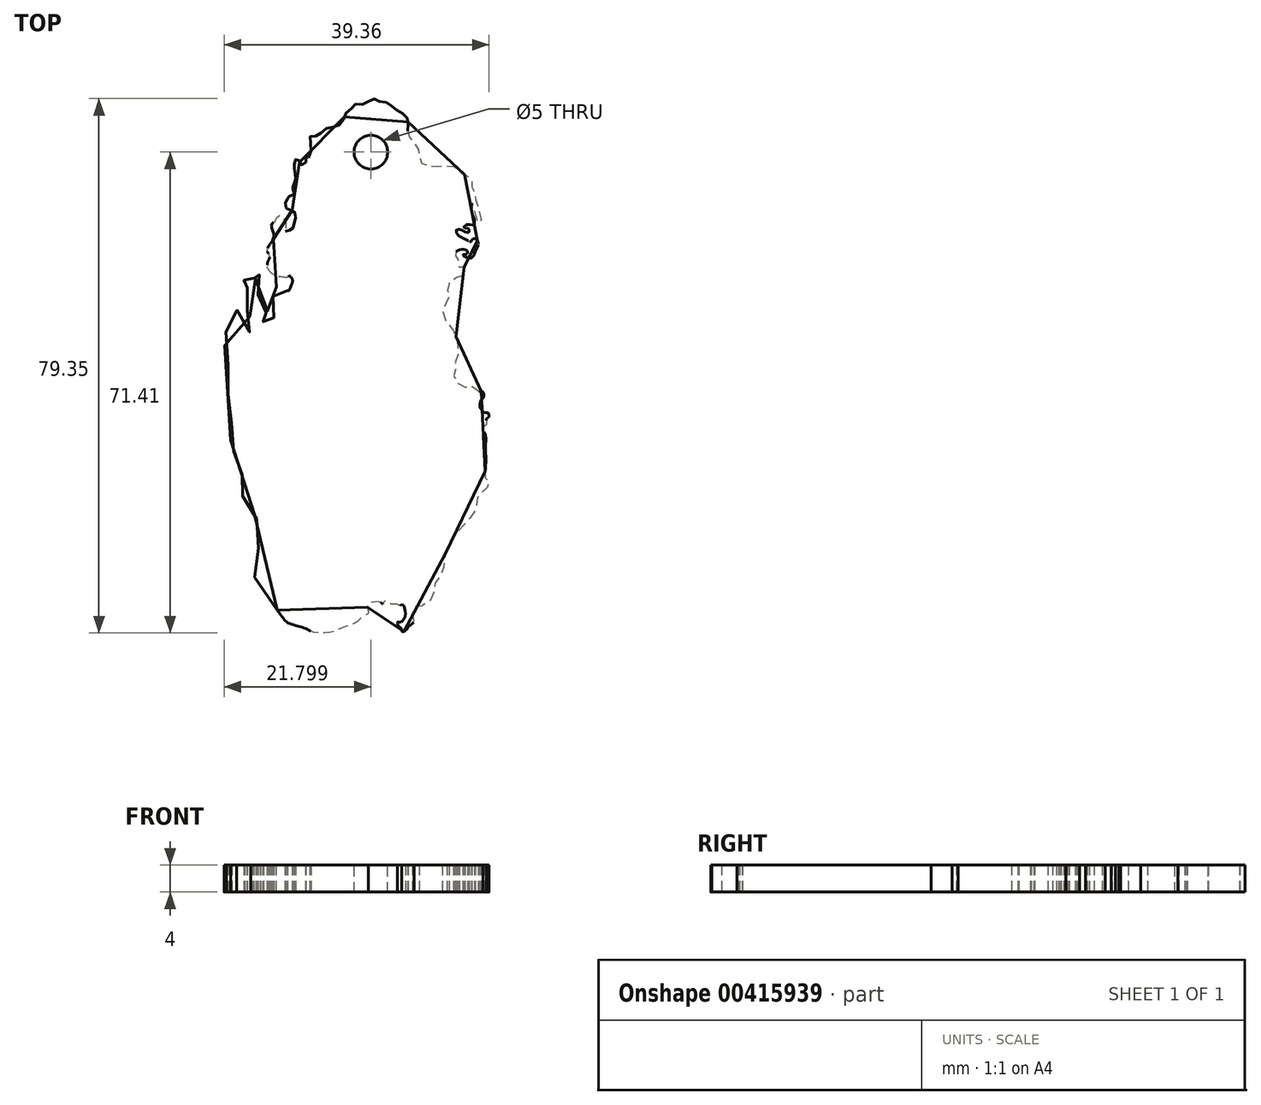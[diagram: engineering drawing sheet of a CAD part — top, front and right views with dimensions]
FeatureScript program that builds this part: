
annotation { "Feature Type Name" : "Feature", "Feature Type Description" : "" }
export const myFeature = defineFeature(function(context is Context, id is Id, definition is map)
    precondition{}
    {
        {
            var Q0;
            Q0=qCreatedBy(makeId("Top.planeOp"),FACE);
            var sketch = newSketch(context, id + "F0", { "sketchPlane" : qUnion([Q0])});
            skFitSpline(sketch, "E0", {"points": [v(-12.7, -36.37) * mm, v(-13.37, -35.26) * mm, v(-14.11, -34.04) * mm, v(-15.15, -32.77) * mm, v(-15.78, -31.92) * mm, v(-16.53, -30.77) * mm, v(-16.68, -30.32) * mm, v(-15.82, -29.47) * mm, v(-15.34, -28.62) * mm, v(-15.23, -27.72) * mm, v(-15.67, -26.9) * mm, v(-15.93, -26.28) * mm, v(-15.67, -25.6) * mm, v(-15.71, -24.87) * mm, v(-15.86, -24.05) * mm, v(-15.78, -23.08) * mm, v(-15.85, -22.68) * mm, v(-16.09, -22.18) * mm, v(-16.59, -21.6) * mm, v(-17.04, -21.1) * mm, v(-17.33, -20.57) * mm, v(-17.57, -19.8) * mm, v(-17.88, -19.43) * mm, v(-18.3, -18.85) * mm, v(-18.6, -18.32) * mm, v(-18.73, -17.72) * mm, v(-18.72, -17.32) * mm, v(-18.63, -16.98) * mm, v(-18.35, -16.53) * mm, v(-18.02, -16.25) * mm, v(-17.73, -15.87) * mm, v(-17.73, -15.4) * mm, v(-17.92, -14.7) * mm, v(-18.17, -14.08) * mm, v(-18.5, -13.6) * mm, v(-18.87, -13.08) * mm, v(-19.3, -12.58) * mm, v(-19.58, -12) * mm, v(-19.63, -11.03) * mm, v(-19.6, -10.14) * mm, v(-19.56, -9.28) * mm, v(-19.45, -8.78) * mm, v(-19.56, -8.51) * mm, v(-19.9, -8.13) * mm, v(-20.18, -7.51) * mm, v(-20.24, -6.57) * mm, v(-20.27, -5.7) * mm, v(-20.15, -4.8) * mm, v(-20, -4.01) * mm, v(-19.87, -3.27) * mm, v(-19.83, -2.2) * mm, v(-19.9, -1.14) * mm, v(-20, -0.58) * mm, v(-20.18, -0.24) * mm, v(-20.02, 0) * mm, v(-20.02, 1.35) * mm, v(-20.24, 2.32) * mm, v(-20.58, 3) * mm, v(-20.61, 3.77) * mm, v(-20.45, 4.76) * mm, v(-19.99, 5.75) * mm, v(-19.92, 6.55) * mm, v(-20.22, 6.64) * mm, v(-20.25, 7.07) * mm, v(-19.65, 7.7) * mm, v(-18.93, 8.1) * mm, v(-18.43, 8.23) * mm, v(-17.97, 7.87) * mm, v(-17.57, 6.94) * mm, v(-17.27, 6.31) * mm, v(-17.2, 5.69) * mm, v(-17.2, 5.12) * mm, v(-16.71, 4.96) * mm, v(-16.28, 5.16) * mm, v(-16.25, 5.52) * mm, v(-16.55, 6.02) * mm, v(-16.71, 6.31) * mm, v(-16.78, 7.07) * mm, v(-16.98, 7.77) * mm, v(-17.24, 8.1) * mm, v(-17.54, 8.3) * mm, v(-17.3, 8.9) * mm, v(-17.08, 9.35) * mm, v(-16.86, 9.86) * mm, v(-16.83, 10.44) * mm, v(-17.08, 11.16) * mm, v(-17.2, 11.6) * mm, v(-17.2, 11.93) * mm, v(-17.59, 11.85) * mm, v(-18, 11.7) * mm, v(-18.5, 11.67) * mm, v(-18.69, 11.93) * mm, v(-18.48, 12.36) * mm, v(-17.96, 12.57) * mm, v(-17.4, 12.71) * mm, v(-16.9, 12.69) * mm, v(-16.6, 12.55) * mm, v(-16.35, 12.23) * mm, v(-16.1, 12.07) * mm, v(-15.9, 12.14) * mm, v(-15.62, 12.31) * mm, v(-15.76, 12.65) * mm, v(-16.14, 13.03) * mm, v(-16.46, 13.3) * mm, v(-16.48, 13.97) * mm, v(-16.42, 14.4) * mm, v(-16.25, 14.4) * mm, v(-16.16, 14.1) * mm, v(-15.94, 13.89) * mm, v(-15.69, 13.74) * mm, v(-15.55, 13.53) * mm, v(-15.2, 13.47) * mm, v(-14.94, 13.47) * mm, v(-14.8, 12.85) * mm, v(-14.77, 12.3) * mm, v(-15.02, 11.76) * mm, v(-15.4, 11.2) * mm, v(-15.58, 10.82) * mm, v(-15.6, 10.44) * mm, v(-15.47, 10.32) * mm, v(-15.35, 10.36) * mm, v(-15.22, 9.95) * mm, v(-15.24, 9.36) * mm, v(-15.28, 8.85) * mm, v(-15.19, 8.44) * mm, v(-14.86, 8.04) * mm, v(-14.46, 7.87) * mm, v(-14.15, 7.94) * mm, v(-14.23, 8.26) * mm, v(-14.01, 8.36) * mm, v(-13.83, 7.99) * mm, v(-13.8, 7.7) * mm, v(-14.05, 7.33) * mm, v(-14.41, 7.02) * mm, v(-14.7, 6.78) * mm, v(-14.86, 6.2) * mm, v(-14.74, 5.88) * mm, v(-14.21, 6.05) * mm, v(-13.76, 5.94) * mm, v(-13.43, 6.01) * mm, v(-13.52, 6.5) * mm, v(-13.72, 7.02) * mm, v(-13.2, 7.1) * mm, v(-12.95, 7.47) * mm, v(-12.93, 7.74) * mm, v(-13.37, 7.8) * mm, v(-13.45, 8.37) * mm, v(-13.39, 9) * mm, v(-13.39, 9.73) * mm, v(-13.39, 10.24) * mm, v(-13, 10.85) * mm, v(-12.9, 11.58) * mm, v(-12.64, 12.19) * mm, v(-12.1, 12.3) * mm, v(-11.64, 11.95) * mm, v(-11.22, 11.34) * mm, v(-11.05, 11.07) * mm, v(-10.6, 11.96) * mm, v(-10.5, 12.76) * mm, v(-10.89, 13.3) * mm, v(-11.2, 13.08) * mm, v(-11.87, 13.13) * mm, v(-12.88, 13.27) * mm, v(-13.72, 13.86) * mm, v(-14.2, 14.72) * mm, v(-14.07, 15.56) * mm, v(-13.86, 16.08) * mm, v(-14.05, 16.62) * mm, v(-14.2, 17.08) * mm, v(-13.93, 17.84) * mm, v(-13.58, 18.32) * mm, v(-13.29, 18.93) * mm, v(-13.27, 19.6) * mm, v(-13.48, 20.27) * mm, v(-13.6, 20.76) * mm, v(-13.42, 21.15) * mm, v(-13.1, 21.31) * mm, v(-12.97, 21.57) * mm, v(-12.82, 21.95) * mm, v(-12.43, 22.22) * mm, v(-12.07, 22.23) * mm, v(-11.75, 21.86) * mm, v(-11.52, 21.42) * mm, v(-11.48, 20.8) * mm, v(-11.5, 20.24) * mm, v(-11.6, 19.95) * mm, v(-11.28, 19.9) * mm, v(-10.93, 20.06) * mm, v(-10.76, 20.34) * mm, v(-10.43, 20.39) * mm, v(-10.23, 20.82) * mm, v(-10.18, 21.37) * mm, v(-10.06, 21.77) * mm, v(-10, 22.21) * mm, v(-10.12, 22.75) * mm, v(-10.48, 23.07) * mm, v(-11.02, 23.12) * mm, v(-11.33, 23.3) * mm, v(-11.5, 23.67) * mm, v(-11.5, 24.14) * mm, v(-11.29, 24.58) * mm, v(-11.23, 24.91) * mm, v(-11.2, 25.12) * mm, v(-10.72, 25.12) * mm, v(-10.24, 25.37) * mm, v(-10.15, 25.7) * mm, v(-10.21, 25.83) * mm, v(-10.4, 25.94) * mm, v(-10.48, 26.23) * mm, v(-10.4, 26.48) * mm, v(-10.25, 26.91) * mm, v(-10.1, 27.25) * mm, v(-9.98, 27.66) * mm, v(-10, 28.15) * mm, v(-10.03, 28.41) * mm, v(-10.15, 29.02) * mm, v(-10.24, 29.45) * mm, v(-10.2, 29.81) * mm, v(-10.21, 30.14) * mm, v(-10.05, 30.56) * mm, v(-9.67, 30.68) * mm, v(-9.48, 30.42) * mm, v(-9.33, 29.95) * mm, v(-8.96, 29.76) * mm, v(-8.52, 30.15) * mm, v(-8.48, 30.74) * mm, v(-8.48, 31.03) * mm, v(-8.15, 30.84) * mm, v(-7.88, 31.25) * mm, v(-7.7, 31.95) * mm, v(-7.78, 32.77) * mm, v(-7.82, 33.43) * mm, v(-7.87, 33.97) * mm, v(-7.75, 34.12) * mm, v(-7.15, 34.07) * mm, v(-6.76, 34.17) * mm, v(-6.3, 34.5) * mm, v(-5.88, 34.92) * mm, v(-5.37, 35.25) * mm, v(-4.88, 35.38) * mm, v(-4.26, 35.42) * mm, v(-3.68, 35.65) * mm, v(-3.2, 35.94) * mm, v(-2.88, 36.6) * mm, v(-2.72, 37.1) * mm, v(-2.44, 37.56) * mm, v(-1.96, 37.9) * mm, v(-1.48, 38.5) * mm, v(-1.27, 38.74) * mm, v(-0.74, 38.88) * mm, v(-0.24, 38.8) * mm, v(0.3, 38.87) * mm, v(0.81, 39.27) * mm, v(1.27, 39.57) * mm, v(1.83, 39.58) * mm, v(2.17, 39.32) * mm, v(2.52, 39.18) * mm, v(3.18, 39.09) * mm, v(3.69, 39.03) * mm, v(4.18, 38.64) * mm, v(4.64, 38.27) * mm, v(4.96, 38) * mm, v(5.44, 37.67) * mm, v(5.93, 37.38) * mm, v(6.32, 37.1) * mm, v(6.63, 36.6) * mm, v(6.7, 36.09) * mm, v(6.67, 35.65) * mm, v(6.66, 35.08) * mm, v(6.66, 34.57) * mm, v(6.85, 34.02) * mm, v(7.36, 33.31) * mm, v(7.93, 32.67) * mm, v(8.28, 32) * mm, v(8.38, 31.3) * mm, v(8.42, 30.53) * mm, v(8.8, 29.97) * mm, v(9.48, 29.72) * mm, v(10.28, 29.59) * mm, v(11.53, 29.6) * mm, v(12.65, 29.66) * mm, v(13.37, 29.58) * mm, v(14.07, 29.3) * mm, v(14.34, 29) * mm, v(14.26, 28.77) * mm, v(14.6, 28.53) * mm, v(15.19, 28.29) * mm, v(15.73, 28) * mm, v(16.07, 27.55) * mm, v(16.17, 27.1) * mm, v(16.18, 26.58) * mm, v(16.37, 26.02) * mm, v(16.66, 25.43) * mm, v(16.62, 24.92) * mm, v(17.06, 23.77) * mm, v(17.22, 23) * mm, v(17.34, 22.51) * mm, v(17.45, 22) * mm, v(17.5, 21.7) * mm, v(17.5, 21.21) * mm, v(17.12, 21.15) * mm, v(16.93, 21.65) * mm, v(16.72, 22.48) * mm, v(16.55, 23.4) * mm, v(16.3, 23.95) * mm, v(16.18, 24.11) * mm, v(16.08, 23.66) * mm, v(16.1, 23.08) * mm, v(16.3, 22.26) * mm, v(16.5, 21.82) * mm, v(16.55, 21.24) * mm, v(16.44, 20.93) * mm, v(16.06, 20.9) * mm, v(15.68, 20.96) * mm, v(15.13, 20.81) * mm, v(14.98, 20.42) * mm, v(15.38, 20.4) * mm, v(15.62, 20.36) * mm, v(15.76, 20.02) * mm, v(15.65, 19.74) * mm, v(15.18, 19.86) * mm, v(14.62, 20.13) * mm, v(14.16, 20.23) * mm, v(13.85, 20.1) * mm, v(13.83, 19.75) * mm, v(14.32, 19.23) * mm, v(14.83, 18.93) * mm, v(15.48, 18.6) * mm, v(16.01, 18.4) * mm, v(16.25, 18.75) * mm, v(16.57, 18.84) * mm, v(16.9, 18.7) * mm, v(17.1, 18.3) * mm, v(17.12, 17.9) * mm, v(16.89, 17.36) * mm, v(16.6, 16.77) * mm, v(16.4, 16.27) * mm, v(15.98, 15.95) * mm, v(15.45, 16.04) * mm, v(14.86, 16.46) * mm, v(15.23, 16.51) * mm, v(15.53, 16.77) * mm, v(15.32, 17.13) * mm, v(14.77, 17.23) * mm, v(14.14, 17.12) * mm, v(13.72, 16.84) * mm, v(13.51, 16.5) * mm, v(13.74, 16.5) * mm, v(13.76, 16.14) * mm, v(14.22, 16.17) * mm, v(14.17, 15.71) * mm, v(14.11, 15.1) * mm, v(14.07, 14.68) * mm, v(14.38, 14.74) * mm, v(14.88, 15.02) * mm, v(15.02, 14.7) * mm, v(15.12, 14.39) * mm, v(15.15, 13.92) * mm, v(14.94, 13.23) * mm, v(14.45, 13.04) * mm, v(13.68, 13) * mm, v(13.15, 12.65) * mm, v(12.72, 12.07) * mm, v(12.5, 11.53) * mm, v(12.5, 11.3) * mm, v(12.6, 11.06) * mm, v(12.77, 10.9) * mm, v(12.8, 10.64) * mm, v(12.82, 10.38) * mm, v(12.7, 9.95) * mm, v(12.43, 9.42) * mm, v(12.17, 8.92) * mm, v(11.86, 8.37) * mm, v(11.8, 7.56) * mm, v(12.2, 6.75) * mm, v(13.04, 5.68) * mm, v(13.52, 4.97) * mm, v(13.87, 4.22) * mm, v(14.1, 3.36) * mm, v(14.2, 3.14) * mm, v(14.11, 2.84) * mm, v(13.95, 2.66) * mm, v(14.03, 2.07) * mm, v(14.16, 1.66) * mm, v(14.04, 1.15) * mm, v(13.72, 0.44) * mm, v(13.6, 0.1) * mm, v(13.61, -0.27) * mm, v(13.78, -0.59) * mm, v(13.8, -1) * mm, v(13.6, -1.31) * mm, v(13.45, -1.66) * mm, v(13.53, -2.22) * mm, v(13.95, -2.58) * mm, v(14.7, -2.97) * mm, v(15.19, -3.24) * mm, v(15.49, -3.16) * mm, v(15.83, -3) * mm, v(16.33, -3.15) * mm, v(16.93, -3.56) * mm, v(17.3, -3.85) * mm, v(17.67, -3.86) * mm, v(17.88, -4.12) * mm, v(17.9, -4.77) * mm, v(17.6, -5.04) * mm, v(17.37, -5.56) * mm, v(17.48, -6.45) * mm, v(17.9, -6.89) * mm, v(18.22, -7) * mm, v(18.55, -7.02) * mm, v(18.73, -7.41) * mm, v(18.61, -7.72) * mm, v(18.33, -7.96) * mm, v(18.32, -8.56) * mm, v(18.27, -8.87) * mm, v(17.96, -9.03) * mm, v(17.84, -9.42) * mm, v(17.98, -9.88) * mm, v(18.12, -10.11) * mm, v(18.23, -10.75) * mm, v(18.2, -12.03) * mm, v(18.23, -13.68) * mm, v(18.16, -15.51) * mm, v(18.06, -16.28) * mm, v(18.2, -16.85) * mm, v(18.49, -17.1) * mm, v(18.68, -17.23) * mm, v(18.65, -17.58) * mm, v(18.32, -18.28) * mm, v(17.81, -18.74) * mm, v(17.33, -19.15) * mm, v(16.96, -19.67) * mm, v(16.88, -20.4) * mm, v(16.8, -20.98) * mm, v(16.68, -21.43) * mm, v(16.46, -21.83) * mm, v(15.79, -22.78) * mm, v(15.1, -23.52) * mm, v(14.35, -24.41) * mm, v(13.52, -25.26) * mm, v(12.86, -26.42) * mm, v(12.28, -27.65) * mm, v(12.09, -28.87) * mm, v(11.97, -30.03) * mm, v(11.64, -30.92) * mm, v(11, -31.78) * mm, v(10.58, -32.92) * mm, v(10.5, -33.81) * mm, v(10.07, -34.78) * mm, v(9.1, -35.56) * mm, v(8.13, -35.81) * mm, v(7.72, -35.84) * mm, v(7.66, -36.34) * mm, v(7.5, -36.53) * mm, v(7.36, -36.84) * mm, v(7.37, -37.15) * mm, v(7.56, -37.5) * mm, v(7.6, -38) * mm, v(7.3, -38.35) * mm, v(6.7, -38.87) * mm, v(6.34, -39.28) * mm, v(5.97, -39.56) * mm, v(5.74, -39.48) * mm, v(5.7, -39.12) * mm, v(5.48, -38.88) * mm, v(5.16, -38.57) * mm, v(5.13, -38.14) * mm, v(5.56, -38.1) * mm, v(6, -37.8) * mm, v(6.3, -37.12) * mm, v(6.27, -36.47) * mm, v(6.17, -36.04) * mm, v(6.04, -35.6) * mm, v(5.7, -35.54) * mm, v(5.48, -35.66) * mm, v(5.18, -35.53) * mm, v(4.62, -35.48) * mm, v(4.06, -35.4) * mm, v(3.64, -35.13) * mm, v(3.34, -35.02) * mm, v(3.03, -35.21) * mm, v(2.98, -35.45) * mm, v(2.62, -35.2) * mm, v(1.9, -35.1) * mm, v(1, -35.35) * mm, v(0.67, -35.97) * mm, v(0.8, -36.59) * mm, v(0.79, -36.82) * mm, v(0.45, -37.06) * mm, v(-0.15, -37.35) * mm, v(-0.54, -37.75) * mm, v(-1.45, -38.38) * mm, v(-2.59, -38.8) * mm, v(-3.93, -39.34) * mm, v(-4.96, -39.64) * mm, v(-7.06, -39.66) * mm, v(-8.02, -39.33) * mm, v(-8.95, -38.9) * mm, v(-9.87, -38.64) * mm, v(-11.09, -38.26) * mm, v(-11.75, -37.65) * mm, v(-12.36, -36.84) * mm, v(-12.7, -36.37) * mm]});
            skSolve(sketch);
        }
        {
            var Q0;
            Q0=makeQuery(id+"F0.imprint","IMPRINT",FACE,{"disambiguationData":[TD([[makeQuery(id+"F0.imprint","IMPRINT",EDGE,{"derivedFrom":sQuery(id+"F0.wireOp",EDGE,"E0")}),-1.0]])]});
            extrude(context, id + "F1", {"entities" : qUnion([Q0]), "depth" : 4 * mm});
        }
        {
            var Q0;
            Q0=makeQuery(id+"F1.opExtrude","CAP_FACE",FACE,{"disambiguationData":[OSD([sQuery(id+"F0.wireOp",EDGE,"E0")])],"isStart":false});
            var sketch = newSketch(context, id + "F2", { "sketchPlane" : qUnion([Q0])});
            skCircle(sketch, "E1", {"center": v(1.17, 31.7) * mm, "radius": 2.5 * mm});
            skSolve(sketch);
        }
        {
            var Q0;
            Q0=makeQuery(id+"F2.imprint","IMPRINT",FACE,{"disambiguationData":[TD([[makeQuery(id+"F2.imprint","IMPRINT",EDGE,{"derivedFrom":sQuery(id+"F2.wireOp",EDGE,"E1")}),1.0]])]});
            extrude(context, id + "F3", {"entities" : qUnion([Q0]), "operationType" : NewBodyOperationType.REMOVE, "oppositeDirection" : true, "depth" : 25 * mm});
        }
    });
